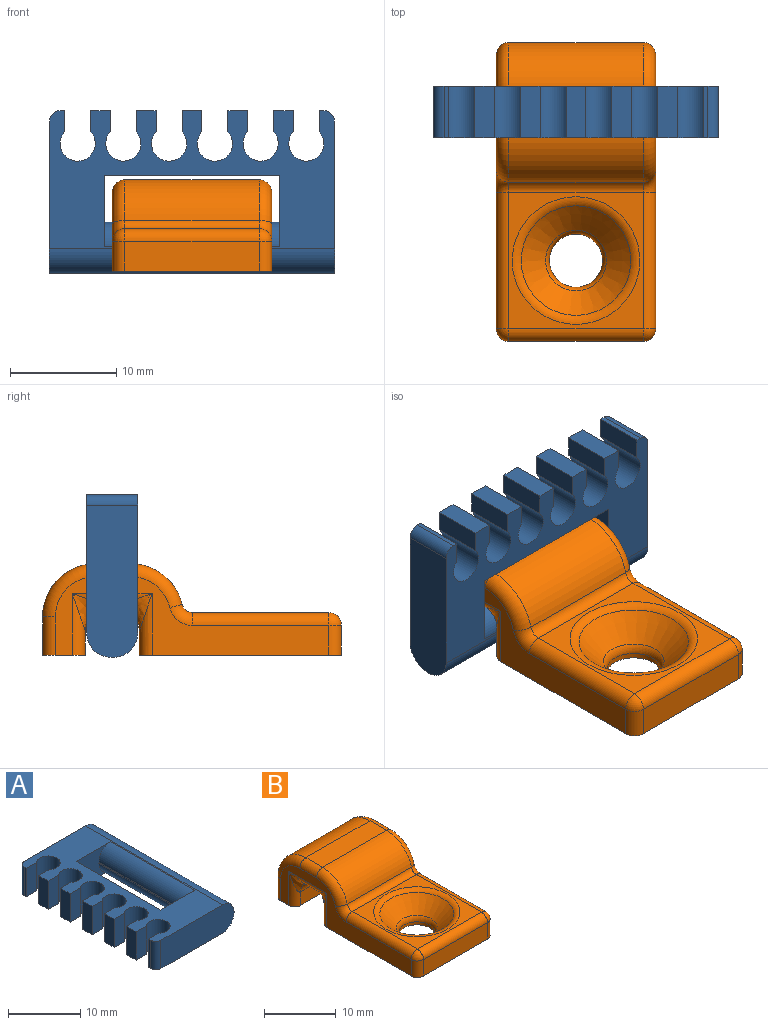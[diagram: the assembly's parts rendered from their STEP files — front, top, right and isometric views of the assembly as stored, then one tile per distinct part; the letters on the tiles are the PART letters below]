
ASSEMBLY  parts=2 mates=1
PART A: 40 faces, bbox 15.3x26.8x4.8 mm
  f0: plane 14.3x4.8mm, normal (0,-1,0), area 66.4mm2, adj f2,f3,f29,f31,f38,f39
  f1: plane 14.3x4.8mm, normal (0,1,0), area 66.4mm2, adj f2,f3,f30,f31,f38,f39
  f2: plane 26.8x13mm, normal (0,0,1), area 162.2mm2, adj f0,f1,f4,f5,f6,f7,f8,f9
  f3: plane 26.8x13mm, normal (0,0,-1), area 162.2mm2, adj f0,f1,f4,f5,f6,f7,f8,f9
  f4: extruded ~4.8x3.3mm, area 36.4mm2, adj f2,f3,f12,f27
  f5: extruded ~4.8x3.3mm, area 36.4mm2, adj f2,f3,f24,f26
  f6: extruded ~4.8x3.3mm, area 36.4mm2, adj f2,f3,f21,f23
  f7: extruded ~4.8x3.3mm, area 36.4mm2, adj f2,f3,f18,f20
  f8: extruded ~4.8x3.3mm, area 36.4mm2, adj f2,f3,f15,f17
  f9: extruded ~4.8x3.3mm, area 36.4mm2, adj f2,f3,f10,f14
  f10: plane 4.8x2mm, normal (0,1,0), area 9.6mm2, adj f2,f3,f9,f11
  f11: plane 4.8x0.42mm, normal (-1,0,0), area 2mm2, adj f2,f3,f10,f29
  f12: plane 4.8x2mm, normal (0,-1,0), area 9.6mm2, adj f2,f3,f4,f13
  f13: plane 4.8x0.42mm, normal (-1,0,0), area 2mm2, adj f2,f3,f12,f30
  f14: plane 4.8x2mm, normal (0,-1,0), area 9.6mm2, adj f2,f3,f9,f16
  f15: plane 4.8x2mm, normal (0,1,0), area 9.6mm2, adj f2,f3,f8,f16
  f16: plane 4.8x1.84mm, normal (-1,0,0), area 8.8mm2, adj f2,f3,f14,f15
  f17: plane 4.8x2mm, normal (0,-1,0), area 9.6mm2, adj f2,f3,f8,f19
  f18: plane 4.8x2mm, normal (0,1,0), area 9.6mm2, adj f2,f3,f7,f19
  f19: plane 4.8x1.84mm, normal (-1,0,0), area 8.8mm2, adj f2,f3,f17,f18
  f20: plane 4.8x2mm, normal (0,-1,0), area 9.6mm2, adj f2,f3,f7,f22
  f21: plane 4.8x2mm, normal (0,1,0), area 9.6mm2, adj f2,f3,f6,f22
  f22: plane 4.8x1.84mm, normal (-1,0,0), area 8.8mm2, adj f2,f3,f20,f21
  f23: plane 4.8x2mm, normal (0,-1,0), area 9.6mm2, adj f2,f3,f6,f25
  f24: plane 4.8x2mm, normal (0,1,0), area 9.6mm2, adj f2,f3,f5,f25
  f25: plane 4.8x1.84mm, normal (-1,0,0), area 8.8mm2, adj f2,f3,f23,f24
  f26: plane 4.8x2mm, normal (0,-1,0), area 9.6mm2, adj f2,f3,f5,f28
  f27: plane 4.8x2mm, normal (0,1,0), area 9.6mm2, adj f2,f3,f4,f28
  f28: plane 4.8x1.84mm, normal (-1,0,0), area 8.8mm2, adj f2,f3,f26,f27
  f29: cylinder r=1mm len=4.8mm, axis (0,0,1), area 7.5mm2, adj f0,f2,f3,f11
  f30: cylinder r=1mm len=4.8mm, axis (0,0,-1), area 7.5mm2, adj f1,f2,f3,f13
  f31: plane 26.8x0.2mm, normal (1,0,0), area 5.4mm2, adj f0,f1,f38,f39
  f32: plane 6.7x4.8mm, normal (0,-1,0), area 23.4mm2, adj f2,f3,f33,f34,f36,f37
  f33: plane 16.5x0.2mm, normal (-1,0,0), area 3.3mm2, adj f32,f35,f36,f37
  f34: plane 16.5x4.8mm, normal (1,0,0), area 79.2mm2, adj f2,f3,f32,f35
  f35: plane 6.7x4.8mm, normal (0,1,0), area 23.4mm2, adj f2,f3,f33,f34,f36,f37
  f36: cylinder r=2.3mm len=16.5mm, axis (0,-1,0), area 59.6mm2, adj f3,f32,f33,f35
  f37: cylinder r=2.3mm len=16.5mm, axis (0,-1,0), area 59.6mm2, adj f2,f32,f33,f35
  f38: cylinder r=2.3mm len=26.8mm, axis (0,-1,0), area 96.8mm2, adj f0,f1,f3,f31
  f39: cylinder r=2.3mm len=26.8mm, axis (0,1,0), area 96.8mm2, adj f0,f1,f2,f31
PART B: 47 faces, bbox 15x28.5x9.4 mm
  f0: plane 12.6x2.8mm, normal (0,-1,0), area 35.3mm2, adj f1,f21,f24,f25
  f1: plane 19x15mm, normal (0,0,-1), area 264.1mm2, adj f0,f2,f9,f10,f14,f21,f24,f35
  f2: plane 12.6x2.3mm, normal (0,1,0), area 29mm2, adj f1,f35,f38,f42
  f3: plane 12.6x0.5mm, normal (0,0,-1), area 6.3mm2, adj f36,f39,f42,f45
  f4: plane 12.6x2.3mm, normal (0,-1,0), area 29mm2, adj f5,f37,f40,f45
  f5: plane 15x4mm, normal (0,0,-1), area 58.8mm2, adj f4,f6,f9,f10,f16,f32,f37,f40
  f6: plane 12.6x3.6mm, normal (0,1,0), area 45.4mm2, adj f5,f12,f16,f32
  f7: plane 12.6x3.27mm, normal (0,0,1), area 41.1mm2, adj f12,f13,f18,f30
  f8: plane 12.8x12.6mm, normal (0,0,1), area 48.3mm2, adj f11,f22,f25,f27,f33
  f9: plane 25.7x7.4mm, normal (1,0,0), area 73mm2, adj f1,f5,f24,f27,f28,f29,f30,f31
  f10: plane 25.7x7.4mm, normal (-1,0,0), area 73mm2, adj f1,f5,f16,f17,f18,f19,f20,f21
  f11: cylinder r=1mm len=12.6mm, axis (1,0,0), area 16.8mm2, adj f8,f13,f20,f28
  f12: cylinder r=5mm len=12.6mm, axis (-1,0,0), area 99mm2, adj f6,f7,f17,f31
  f13: cylinder r=5mm len=12.6mm, axis (1,0,0), area 84.1mm2, adj f7,f11,f19,f29
  f14: cylinder r=2.5mm len=5mm, axis (0,0,1), area 7.9mm2, adj f1,f34
  f15: cone r=2.5mm half-angle=45deg, axis (0,0,1), area 81.6mm2, adj f33,f34
  f16: cylinder r=1.2mm len=3.6mm, axis (0,0,1), area 6.8mm2, adj f5,f6,f10,f17
  f17: torus R=3.8mm, axis (1,0,0), area 13.5mm2, adj f10,f12,f16,f18
  f18: cylinder r=1.2mm len=3.27mm, axis (0,-1,0), area 6.2mm2, adj f7,f10,f17,f19
  f19: torus R=3.8mm, axis (1,0,0), area 11.5mm2, adj f10,f13,f18,f20
  f20: torus R=2.2mm, axis (1,0,0), area 3.6mm2, adj f10,f11,f19,f22
  f21: cylinder r=1.2mm len=2.8mm, axis (0,0,-1), area 5.3mm2, adj f0,f1,f10,f23
  f22: cylinder r=1.2mm len=12.8mm, axis (0,-1,0), area 24.1mm2, adj f8,f10,f20,f23
  f23: sphere r=1.2mm, area 2.3mm2, adj f21,f22,f25
  f24: cylinder r=1.2mm len=2.8mm, axis (0,0,1), area 5.3mm2, adj f0,f1,f9,f26
  f25: cylinder r=1.2mm len=12.6mm, axis (-1,0,0), area 23.8mm2, adj f0,f8,f23,f26
  f26: sphere r=1.2mm, area 2.3mm2, adj f24,f25,f27
  f27: cylinder r=1.2mm len=12.8mm, axis (0,1,0), area 24.1mm2, adj f8,f9,f26,f28
  f28: torus R=2.2mm, axis (1,0,0), area 3.6mm2, adj f9,f11,f27,f29
  f29: torus R=3.8mm, axis (1,0,0), area 11.5mm2, adj f9,f13,f28,f30
  f30: cylinder r=1.2mm len=3.27mm, axis (0,1,0), area 6.2mm2, adj f7,f9,f29,f31
  f31: torus R=3.8mm, axis (1,0,0), area 13.5mm2, adj f9,f12,f30,f32
  f32: cylinder r=1.2mm len=3.6mm, axis (0,0,-1), area 6.8mm2, adj f5,f6,f9,f31
  f33: torus R=6mm, axis (0,0,-1), area 32.9mm2, adj f8,f15
  f34: torus R=3.7mm, axis (0,0,-1), area 15.5mm2, adj f14,f15
  f35: cylinder r=1.2mm len=5.8mm, axis (0,0,1), area 6.7mm2, adj f1,f2,f10,f41
  f36: cylinder r=1.2mm len=7.5mm, axis (0,1,0), area 5.7mm2, adj f3,f10,f41,f44
  f37: cylinder r=1.2mm len=5.8mm, axis (0,0,-1), area 6.7mm2, adj f4,f5,f10,f44
  f38: cylinder r=1.2mm len=5.8mm, axis (0,0,-1), area 6.7mm2, adj f1,f2,f9,f43
  f39: cylinder r=1.2mm len=7.5mm, axis (0,-1,0), area 5.7mm2, adj f3,f9,f43,f46
  f40: cylinder r=1.2mm len=5.8mm, axis (0,0,1), area 6.7mm2, adj f4,f5,f9,f46
  f41: bspline ~3.5x3.5mm, area 5.6mm2, adj f35,f36,f42
  f42: cylinder r=2.3mm len=12.6mm, axis (1,0,0), area 45.5mm2, adj f2,f3,f41,f43
  f43: bspline ~3.5x3.5mm, area 5.6mm2, adj f38,f39,f42
  f44: bspline ~3.5x3.5mm, area 5.6mm2, adj f36,f37,f45
  f45: cylinder r=2.3mm len=12.6mm, axis (1,0,0), area 45.5mm2, adj f3,f4,f44,f46
  f46: bspline ~3.5x3.5mm, area 5.6mm2, adj f39,f40,f45
PLACE A rot(axis=(-0.58,0.58,0.58),120deg) t=(14.5,-16.07,16.61)mm
PLACE B t=(-6.4,-11.12,1.13)mm
MATE fastened A.f33 <-> B.f3  axis (0,0,1) through (1.1,-13.67,8.11)mm
